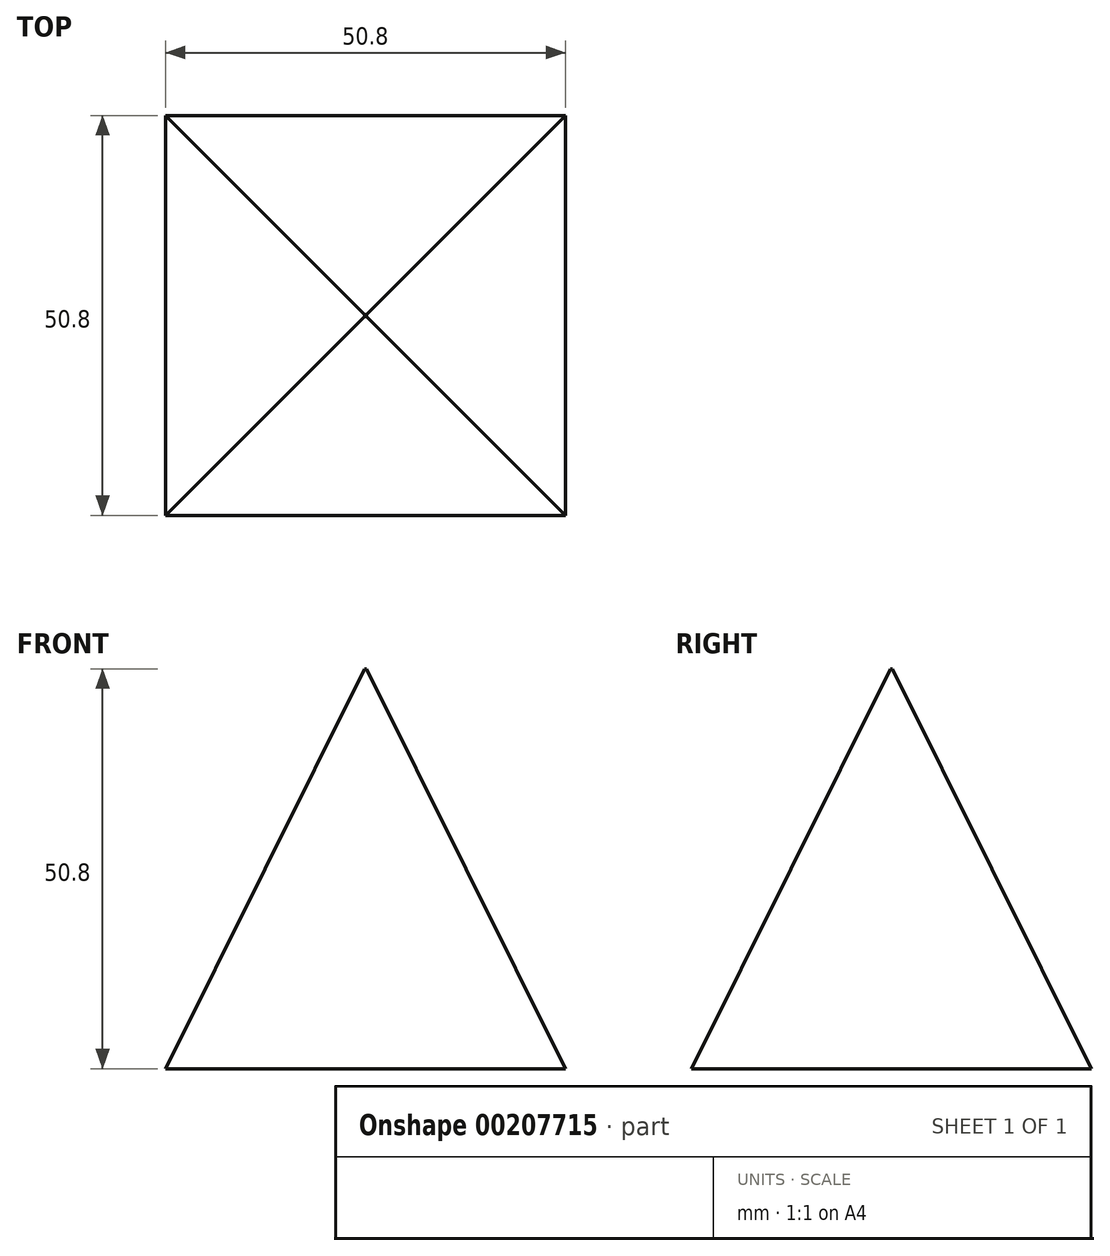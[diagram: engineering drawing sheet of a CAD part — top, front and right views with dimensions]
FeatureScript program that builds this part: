
annotation { "Feature Type Name" : "Feature", "Feature Type Description" : "" }
export const myFeature = defineFeature(function(context is Context, id is Id, definition is map)
    precondition{}
    {
        {
            var Q0;
            Q0=qCreatedBy(makeId("Top.planeOp"),FACE);
            var sketch = newSketch(context, id + "F0", { "sketchPlane" : qUnion([Q0])});
            skLineSegment(sketch, "E0.bottom", {"start": v(25.4, 25.4) * mm, "end": v(-25.4, 25.4) * mm});
            skLineSegment(sketch, "E0.top", {"start": v(25.4, -25.4) * mm, "end": v(-25.4, -25.4) * mm});
            skLineSegment(sketch, "E0.left", {"start": v(25.4, 25.4) * mm, "end": v(25.4, -25.4) * mm});
            skLineSegment(sketch, "E0.right", {"start": v(-25.4, 25.4) * mm, "end": v(-25.4, -25.4) * mm});
            skPoint(sketch, "E0.middle", {"position": v(0, 0) * mm});
            skSolve(sketch);
        }
        {
            var Q0;
            Q0=qCreatedBy(makeId("Top.planeOp"),FACE);
            cPlane(context, id + "F1", {"entities" : qUnion([Q0]), "cplaneType" : CPlaneType.OFFSET, "offset" : 50.8 * mm, "width" : 152.4 * mm, "height" : 152.4 * mm});
        }
        {
            var Q0;
            Q0=qCreatedBy(id+"F1.planeOp",FACE);
            var sketch = newSketch(context, id + "F2", { "sketchPlane" : qUnion([Q0])});
            skLineSegment(sketch, "E1.bottom", {"start": v(0.13, 0.13) * mm, "end": v(-0.13, 0.13) * mm});
            skLineSegment(sketch, "E1.top", {"start": v(0.13, -0.13) * mm, "end": v(-0.13, -0.13) * mm});
            skLineSegment(sketch, "E1.left", {"start": v(0.13, 0.13) * mm, "end": v(0.13, -0.13) * mm});
            skLineSegment(sketch, "E1.right", {"start": v(-0.13, 0.13) * mm, "end": v(-0.13, -0.13) * mm});
            skPoint(sketch, "E1.middle", {"position": v(0, 0) * mm});
            skSolve(sketch);
        }
        {
            var Q0;
            Q0 = qSketchRegion(id + "F2", true);
            var Q1;
            Q1 = qSketchRegion(id + "F0", true);
            loft(context, id + "F3", {"sheetProfilesArray" : [{ "sheetProfileEntities" : qUnion([Q0]) }, { "sheetProfileEntities" : qUnion([Q1]) }]});
        }
    });
